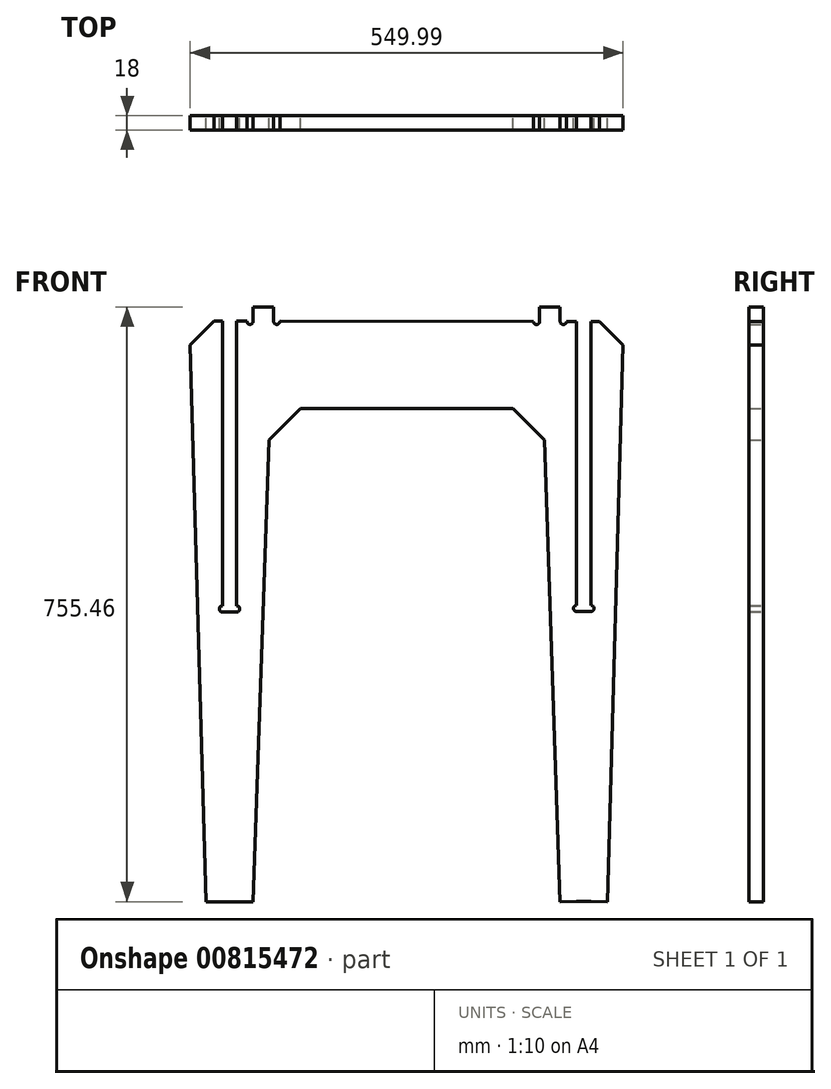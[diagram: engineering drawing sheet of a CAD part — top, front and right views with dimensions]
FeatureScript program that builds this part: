
annotation { "Feature Type Name" : "Feature", "Feature Type Description" : "" }
export const myFeature = defineFeature(function(context is Context, id is Id, definition is map)
    precondition{}
    {
        {
            var Q0;
            Q0=qCreatedBy(makeId("Front.planeOp"),FACE);
            var sketch = newSketch(context, id + "F0", { "sketchPlane" : qUnion([Q0])});
            skPoint(sketch, "E0.middle", {"position": v(0, 0) * mm});
            skLineSegment(sketch, "E1.right", {"start": v(195.01, 379) * mm, "end": v(195.01, 361) * mm});
            skPoint(sketch, "E2.start.orphan", {"position": v(-195, 368.73) * mm});
            skPoint(sketch, "E3.start.orphan", {"position": v(195.01, 370) * mm});
            skLineSegment(sketch, "E4", {"start": v(-203, 361.18) * mm, "end": v(-215.99, 361.18) * mm});
            skPoint(sketch, "E5.orphan", {"position": v(-274.99, 376.28) * mm});
            skLineSegment(sketch, "E6", {"start": v(203.01, 361) * mm, "end": v(216, 361) * mm});
            skPoint(sketch, "E7.orphan", {"position": v(274.99, 376.28) * mm});
            skArc(sketch, "E8", {"start": v(195.01, 361) * mm, "mid": v(199.01, 357) * mm, "end": v(203.01, 361) * mm});
            skArc(sketch, "E9", {"start": v(-203, 361.18) * mm, "mid": v(-199, 357.18) * mm, "end": v(-195, 361.18) * mm});
            skLineSegment(sketch, "E10.top", {"start": v(-244.9, 361.18) * mm, "end": v(-233.99, 361.18) * mm});
            skLineSegment(sketch, "E11", {"start": v(-134.99, 250.34) * mm, "end": v(135, 250.34) * mm});
            skLineSegment(sketch, "E12", {"start": v(-244.9, 361.18) * mm, "end": v(-274.99, 331.07) * mm});
            skLineSegment(sketch, "E13", {"start": v(245, 361) * mm, "end": v(275, 331) * mm});
            skLineSegment(sketch, "E14", {"start": v(-134.99, 250.34) * mm, "end": v(-174.99, 210.34) * mm});
            skLineSegment(sketch, "E15", {"start": v(135, 250.34) * mm, "end": v(175, 210.34) * mm});
            skLineSegment(sketch, "E16", {"start": v(-274.99, 331.07) * mm, "end": v(-254.99, -376.28) * mm});
            skLineSegment(sketch, "E17", {"start": v(-174.99, 210.34) * mm, "end": v(-194.99, -376.28) * mm});
            skPoint(sketch, "E18.start.orphan", {"position": v(-274.99, -376.28) * mm});
            skLineSegment(sketch, "E19", {"start": v(175, 210.34) * mm, "end": v(195, -376.28) * mm});
            skLineSegment(sketch, "E20", {"start": v(275, 331) * mm, "end": v(255, -376.28) * mm});
            skPoint(sketch, "E21.start.orphan", {"position": v(274.99, -376.28) * mm});
            skPoint(sketch, "E22.left.end.orphan", {"position": v(-195, 361.18) * mm});
            skPoint(sketch, "E23.orphan", {"position": v(-195, 376.28) * mm});
            skLineSegment(sketch, "E24", {"start": v(-195, 361.18) * mm, "end": v(-195, 379.18) * mm});
            skLineSegment(sketch, "E25", {"start": v(-195, 379.18) * mm, "end": v(-169, 379.18) * mm});
            skLineSegment(sketch, "E26", {"start": v(-169, 379.18) * mm, "end": v(-169, 361.18) * mm});
            skLineSegment(sketch, "E27", {"start": v(-254.99, -376.28) * mm, "end": v(-233.99, -376.28) * mm});
            skLineSegment(sketch, "E28.bottom", {"start": v(-233.99, -376.28) * mm, "end": v(-215.99, -376.28) * mm});
            skLineSegment(sketch, "E28.top", {"start": v(-233.99, -8.28) * mm, "end": v(-215.99, -8.28) * mm});
            skLineSegment(sketch, "E29", {"start": v(255, -376.28) * mm, "end": v(234, -375.69) * mm});
            skLineSegment(sketch, "E30.bottom", {"start": v(234, -375.69) * mm, "end": v(216, -375.69) * mm});
            skLineSegment(sketch, "E30.top", {"start": v(234, -7.69) * mm, "end": v(216, -7.69) * mm});
            skLineSegment(sketch, "E31", {"start": v(195.01, 379) * mm, "end": v(169.01, 379) * mm});
            skLineSegment(sketch, "E32", {"start": v(169.01, 379) * mm, "end": v(169.01, 361) * mm});
            skLineSegment(sketch, "E33", {"start": v(-161, 361.18) * mm, "end": v(161.01, 361) * mm});
            skArc(sketch, "E34", {"start": v(-169, 361.18) * mm, "mid": v(-165, 357.18) * mm, "end": v(-161, 361.18) * mm});
            skLineSegment(sketch, "E35", {"start": v(-215.99, -376.28) * mm, "end": v(-194.99, -376.28) * mm});
            skLineSegment(sketch, "E36", {"start": v(195, -376.28) * mm, "end": v(216, -375.69) * mm});
            skArc(sketch, "E37", {"start": v(161.01, 361) * mm, "mid": v(165.01, 357) * mm, "end": v(169.01, 361) * mm});
            skLineSegment(sketch, "E38", {"start": v(-274.99, 331.07) * mm, "end": v(-274.99, 376.28) * mm});
            skArc(sketch, "E39", {"start": v(-233.99, -0.28) * mm, "mid": v(-237.99, -4.28) * mm, "end": v(-233.99, -8.28) * mm});
            skArc(sketch, "E40", {"start": v(-215.99, -8.28) * mm, "mid": v(-211.99, -4.28) * mm, "end": v(-215.99, -0.28) * mm});
            skLineSegment(sketch, "E41.trimOffspring", {"start": v(-233.99, -0.28) * mm, "end": v(-233.99, 361.18) * mm});
            skLineSegment(sketch, "E42.trimOffspring", {"start": v(-215.99, -0.28) * mm, "end": v(-215.99, 361.18) * mm});
            skLineSegment(sketch, "E43.trimOffspring", {"start": v(-215.99, 361.18) * mm, "end": v(-203, 361.18) * mm});
            skLineSegment(sketch, "E44.trimOffspring", {"start": v(-233.99, 361.18) * mm, "end": v(-244.9, 361.18) * mm});
            skArc(sketch, "E45", {"start": v(234, -7.69) * mm, "mid": v(238, -3.69) * mm, "end": v(234, 0.31) * mm});
            skArc(sketch, "E46", {"start": v(216, 0.31) * mm, "mid": v(212, -3.69) * mm, "end": v(216, -7.69) * mm});
            skLineSegment(sketch, "E47.trimOffspring", {"start": v(216, 0.31) * mm, "end": v(216, 361) * mm});
            skLineSegment(sketch, "E48.trimOffspring", {"start": v(234, 0.31) * mm, "end": v(234, 361) * mm});
            skLineSegment(sketch, "E49.trimOffspring", {"start": v(234, 361) * mm, "end": v(245, 361) * mm});
            skLineSegment(sketch, "E50", {"start": v(-233.99, 361.18) * mm, "end": v(-233.99, 384.12) * mm});
            skSolve(sketch);
        }
        {
            var Q0;
            Q0=makeQuery(id+"F0.imprint","IMPRINT",FACE,{"disambiguationData":[TD([[makeQuery(id+"F0.imprint","IMPRINT",EDGE,{"derivedFrom":sQuery(id+"F0.wireOp",EDGE,"E1.right")}),-1.0]])]});
            extrude(context, id + "F1", {"entities" : qUnion([Q0]), "depth" : 18 * mm, "offsetDistance" : 25 * mm});
        }
    });
